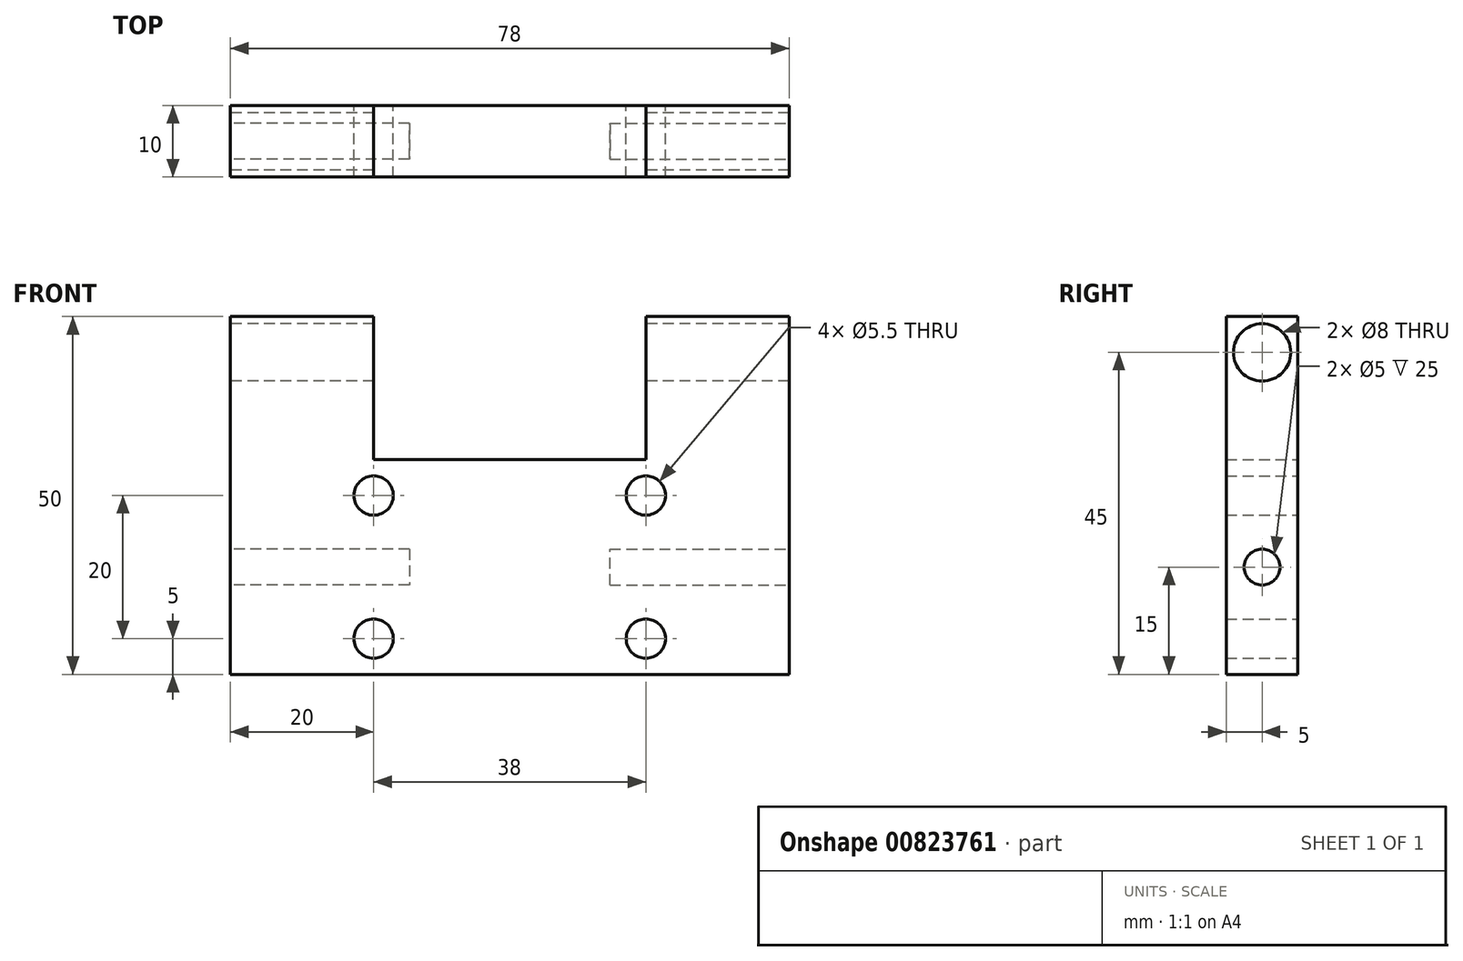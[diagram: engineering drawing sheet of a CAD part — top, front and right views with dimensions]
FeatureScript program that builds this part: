
annotation { "Feature Type Name" : "Feature", "Feature Type Description" : "" }
export const myFeature = defineFeature(function(context is Context, id is Id, definition is map)
    precondition{}
    {
        {
            var Q0;
            Q0=qCreatedBy(makeId("Front.planeOp"),FACE);
            var sketch = newSketch(context, id + "F0", { "sketchPlane" : qUnion([Q0])});
            skLineSegment(sketch, "E0.bottom", {"start": v(-39, 24) * mm, "end": v(-19, 24) * mm});
            skPoint(sketch, "E0.middle", {"position": v(0, 0) * mm});
            skPoint(sketch, "E1.start.orphan", {"position": v(-19, 24) * mm});
            skLineSegment(sketch, "E2.trimOffspring", {"start": v(19, 24) * mm, "end": v(39, 24) * mm});
            skPoint(sketch, "E3.top.start.orphan", {"position": v(-19, 4) * mm});
            skLineSegment(sketch, "E4.top", {"start": v(19, 4) * mm, "end": v(-19, 4) * mm});
            skLineSegment(sketch, "E4.left", {"start": v(19, 24) * mm, "end": v(19, 4) * mm});
            skLineSegment(sketch, "E4.right", {"start": v(-19, 24) * mm, "end": v(-19, 4) * mm});
            skCircle(sketch, "E5", {"center": v(-19, -1) * mm, "radius": 2.75 * mm});
            skCircle(sketch, "E6", {"center": v(19, -1) * mm, "radius": 2.75 * mm});
            skLineSegment(sketch, "E7.top", {"start": v(-39, -26) * mm, "end": v(39, -26) * mm});
            skLineSegment(sketch, "E8", {"start": v(-39, 24) * mm, "end": v(-39, -26) * mm});
            skLineSegment(sketch, "E9", {"start": v(39, 24) * mm, "end": v(39, -26) * mm});
            skCircle(sketch, "E10", {"center": v(-19, -21) * mm, "radius": 2.75 * mm});
            skCircle(sketch, "E11", {"center": v(19, -21) * mm, "radius": 2.75 * mm});
            skSolve(sketch);
        }
        {
            var Q0;
            Q0=makeQuery(id+"F0.imprint","IMPRINT",FACE,{"disambiguationData":[TD([[makeQuery(id+"F0.imprint","IMPRINT",EDGE,{"derivedFrom":sQuery(id+"F0.wireOp",EDGE,"E0.bottom")}),-1.0]])]});
            extrude(context, id + "F1", {"entities" : qUnion([Q0]), "depth" : 10 * mm, "offsetDistance" : 25 * mm});
        }
        {
            var Q0;
            Q0=makeQuery(id+"F1.opExtrude","SWEPT_FACE",FACE,{"disambiguationData":[OSD([sQuery(id+"F0.wireOp",EDGE,"E8")])]});
            var sketch = newSketch(context, id + "F2", { "sketchPlane" : qUnion([Q0])});
            skCircle(sketch, "E12", {"center": v(5, 19) * mm, "radius": 4 * mm});
            skPoint(sketch, "E12.centerSnap0", {"position": v(5, 24) * mm});
            skSolve(sketch);
        }
        {
            var Q0;
            Q0 = qSketchRegion(id + "F2", true);
            extrude(context, id + "F3", {"entities" : qUnion([Q0]), "operationType" : NewBodyOperationType.REMOVE, "oppositeDirection" : true, "depth" : 99 * mm, "offsetDistance" : 25 * mm});
        }
        {
            var Q0;
            Q0=makeQuery(id+"F1.opExtrude","SWEPT_FACE",FACE,{"disambiguationData":[OSD([sQuery(id+"F0.wireOp",EDGE,"E8")])]});
            var sketch = newSketch(context, id + "F4", { "sketchPlane" : qUnion([Q0])});
            skCircle(sketch, "E13", {"center": v(5, -11) * mm, "radius": 2.5 * mm});
            skPoint(sketch, "E13.centerSnap0", {"position": v(5, -26) * mm});
            skSolve(sketch);
        }
        {
            var Q0;
            Q0 = qSketchRegion(id + "F4", true);
            extrude(context, id + "F5", {"entities" : qUnion([Q0]), "operationType" : NewBodyOperationType.REMOVE, "oppositeDirection" : true, "depth" : 25 * mm, "offsetDistance" : 25 * mm});
        }
        {
            var Q0;
            Q0=makeQuery(id+"F1.opExtrude","SWEPT_FACE",FACE,{"disambiguationData":[OSD([sQuery(id+"F0.wireOp",EDGE,"E9")])]});
            var sketch = newSketch(context, id + "F6", { "sketchPlane" : qUnion([Q0])});
            skCircle(sketch, "E14", {"center": v(-5, -11) * mm, "radius": 2.5 * mm});
            skPoint(sketch, "E14.centerSnap0", {"position": v(-5, -26) * mm});
            skSolve(sketch);
        }
        {
            var Q0;
            Q0 = qSketchRegion(id + "F6", true);
            extrude(context, id + "F7", {"entities" : qUnion([Q0]), "operationType" : NewBodyOperationType.REMOVE, "oppositeDirection" : true, "depth" : 25 * mm, "offsetDistance" : 25 * mm});
        }
        {
            var Q0;
            Q0=makeQuery(id+"F1.opExtrude","SWEPT_FACE",FACE,{"disambiguationData":[OSD([sQuery(id+"F0.wireOp",EDGE,"E9")])]});
            var sketch = newSketch(context, id + "F8", { "sketchPlane" : qUnion([Q0])});
            skSolve(sketch);
        }
        {
            var Q0;
            Q0 = qSketchRegion(id + "F2", true);
            extrude(context, id + "F9", {"entities" : qUnion([Q0]), "operationType" : NewBodyOperationType.REMOVE, "oppositeDirection" : true, "depth" : 75 * mm, "offsetDistance" : 25 * mm});
        }
    });
